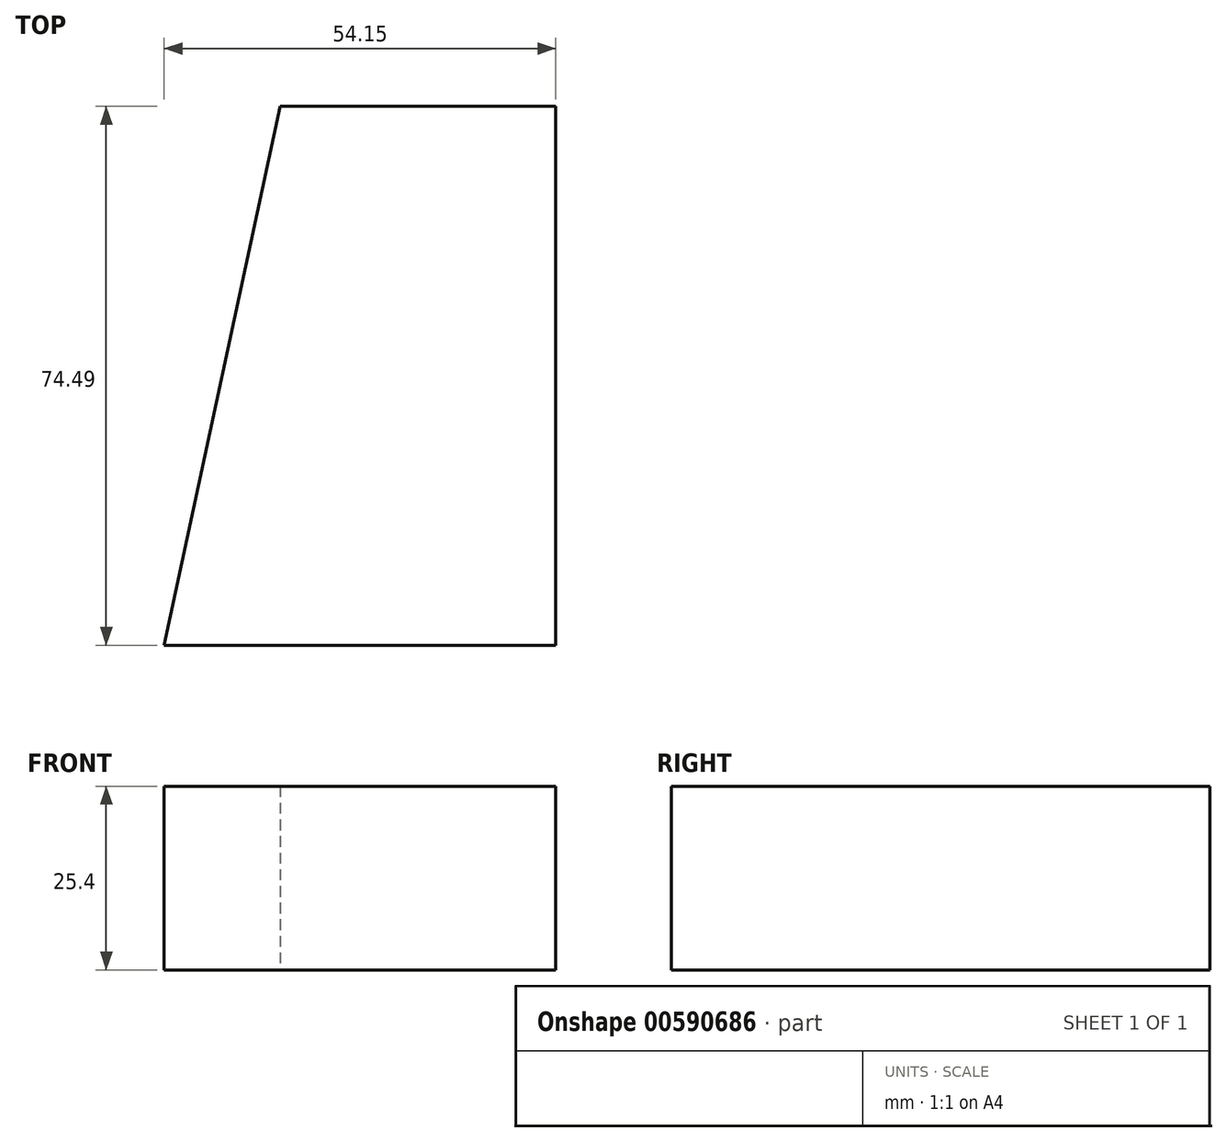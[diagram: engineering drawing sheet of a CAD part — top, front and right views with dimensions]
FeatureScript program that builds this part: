
annotation { "Feature Type Name" : "Feature", "Feature Type Description" : "" }
export const myFeature = defineFeature(function(context is Context, id is Id, definition is map)
    precondition{}
    {
        {
            var Q0;
            Q0=qCreatedBy(makeId("Top.planeOp"),FACE);
            var sketch = newSketch(context, id + "F0", { "sketchPlane" : qUnion([Q0])});
            skLineSegment(sketch, "E0", {"start": v(-48.48, -68.42) * mm, "end": v(2.32, -68.42) * mm});
            skLineSegment(sketch, "E1", {"start": v(2.32, -68.42) * mm, "end": v(18.37, 6.07) * mm});
            skLineSegment(sketch, "E2", {"start": v(18.37, 6.07) * mm, "end": v(56.47, 6.07) * mm});
            skLineSegment(sketch, "E3", {"start": v(56.47, 6.07) * mm, "end": v(56.47, -68.42) * mm});
            skLineSegment(sketch, "E4", {"start": v(56.47, -68.42) * mm, "end": v(2.32, -68.42) * mm});
            skSolve(sketch);
        }
        {
            var Q0;
            Q0=makeQuery(id+"F0.imprint","IMPRINT",FACE,{"disambiguationData":[TD([[makeQuery(id+"F0.imprint","IMPRINT",EDGE,{"derivedFrom":sQuery(id+"F0.wireOp",EDGE,"E1")}),-1.0]])]});
            extrude(context, id + "F1", {"entities" : qUnion([Q0]), "depth" : 25.4 * mm, "offsetDistance" : 25.4 * mm});
        }
    });
